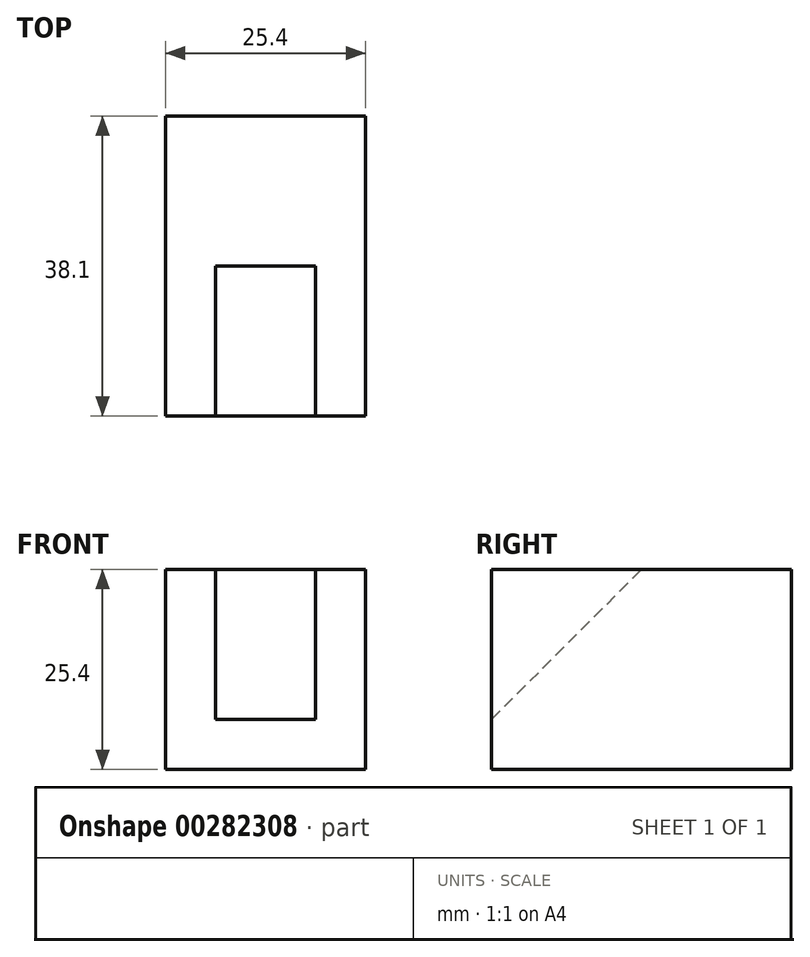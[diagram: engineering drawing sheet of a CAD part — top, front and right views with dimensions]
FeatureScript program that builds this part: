
annotation { "Feature Type Name" : "Feature", "Feature Type Description" : "" }
export const myFeature = defineFeature(function(context is Context, id is Id, definition is map)
    precondition{}
    {
        {
            var Q0;
            Q0=qCreatedBy(makeId("Front.planeOp"),FACE);
            var sketch = newSketch(context, id + "F0", { "sketchPlane" : qUnion([Q0])});
            skLineSegment(sketch, "E0", {"start": v(0, 0) * mm, "end": v(6.35, 0) * mm});
            skLineSegment(sketch, "E1", {"start": v(6.35, 0) * mm, "end": v(6.35, 25.4) * mm});
            skLineSegment(sketch, "E2", {"start": v(6.35, 25.4) * mm, "end": v(0, 25.4) * mm});
            skLineSegment(sketch, "E3", {"start": v(0, 25.4) * mm, "end": v(0, 0) * mm});
            skSolve(sketch);
        }
        {
            var Q0;
            Q0 = qSketchRegion(id + "F0", true);
            extrude(context, id + "F1", {"entities" : qUnion([Q0]), "depth" : 38.1 * mm});
        }
        {
            var Q0;
            Q0=makeQuery(id+"F1.opExtrude","SWEPT_FACE",FACE,{"disambiguationData":[OSD([sQuery(id+"F0.wireOp",EDGE,"E1")])]});
            var sketch = newSketch(context, id + "F2", { "sketchPlane" : qUnion([Q0])});
            skLineSegment(sketch, "E4", {"start": v(0, 25.4) * mm, "end": v(-19.05, 25.4) * mm});
            skLineSegment(sketch, "E5", {"start": v(-19.05, 25.4) * mm, "end": v(-19.05, 0) * mm});
            skLineSegment(sketch, "E6", {"start": v(-19.05, 0) * mm, "end": v(0, 0) * mm});
            skLineSegment(sketch, "E7", {"start": v(0, 0) * mm, "end": v(0, 25.4) * mm});
            skSolve(sketch);
        }
        {
            var Q0;
            Q0 = qSketchRegion(id + "F2", true);
            extrude(context, id + "F3", {"entities" : qUnion([Q0]), "operationType" : NewBodyOperationType.ADD, "depth" : 19.05 * mm});
        }
        {
            var Q0;
            Q0=makeQuery(id+"F3.opExtrude","SWEPT_FACE",FACE,{"disambiguationData":[OSD([sQuery(id+"F2.wireOp",EDGE,"E5")])]});
            var sketch = newSketch(context, id + "F4", { "sketchPlane" : qUnion([Q0])});
            skLineSegment(sketch, "E8", {"start": v(6.35, 6.35) * mm, "end": v(25.4, 6.35) * mm});
            skLineSegment(sketch, "E9", {"start": v(25.4, 6.35) * mm, "end": v(25.4, 0) * mm});
            skLineSegment(sketch, "E10", {"start": v(25.4, 0) * mm, "end": v(6.35, 0) * mm});
            skLineSegment(sketch, "E11", {"start": v(6.35, 0) * mm, "end": v(6.35, 6.35) * mm});
            skSolve(sketch);
        }
        {
            var Q0;
            Q0 = qSketchRegion(id + "F4", true);
            extrude(context, id + "F5", {"entities" : qUnion([Q0]), "operationType" : NewBodyOperationType.ADD, "depth" : 19.05 * mm});
        }
        {
            var Q0;
            Q0=makeQuery(id+"F1.opExtrude","SWEPT_FACE",FACE,{"disambiguationData":[OSD([sQuery(id+"F0.wireOp",EDGE,"E1")])]});
            var sketch = newSketch(context, id + "F6", { "sketchPlane" : qUnion([Q0])});
            skLineSegment(sketch, "E12", {"start": v(-38.1, 6.35) * mm, "end": v(-19.05, 25.4) * mm});
            skLineSegment(sketch, "E13", {"start": v(-19.05, 25.4) * mm, "end": v(-19.05, 6.35) * mm});
            skLineSegment(sketch, "E14", {"start": v(-19.05, 6.35) * mm, "end": v(-38.1, 6.35) * mm});
            skSolve(sketch);
        }
        {
            var Q0;
            Q0 = qSketchRegion(id + "F6", true);
            extrude(context, id + "F7", {"entities" : qUnion([Q0]), "operationType" : NewBodyOperationType.ADD, "depth" : 12.7 * mm});
        }
        {
            var Q0;
            Q0=makeQuery(id+"F3.opExtrude","SWEPT_FACE",FACE,{"disambiguationData":[OSD([sQuery(id+"F2.wireOp",EDGE,"E5")])]});
            extrude(context, id + "F8", {"entities" : qUnion([Q0]), "operationType" : NewBodyOperationType.ADD, "depth" : 19.05 * mm});
        }
    });
